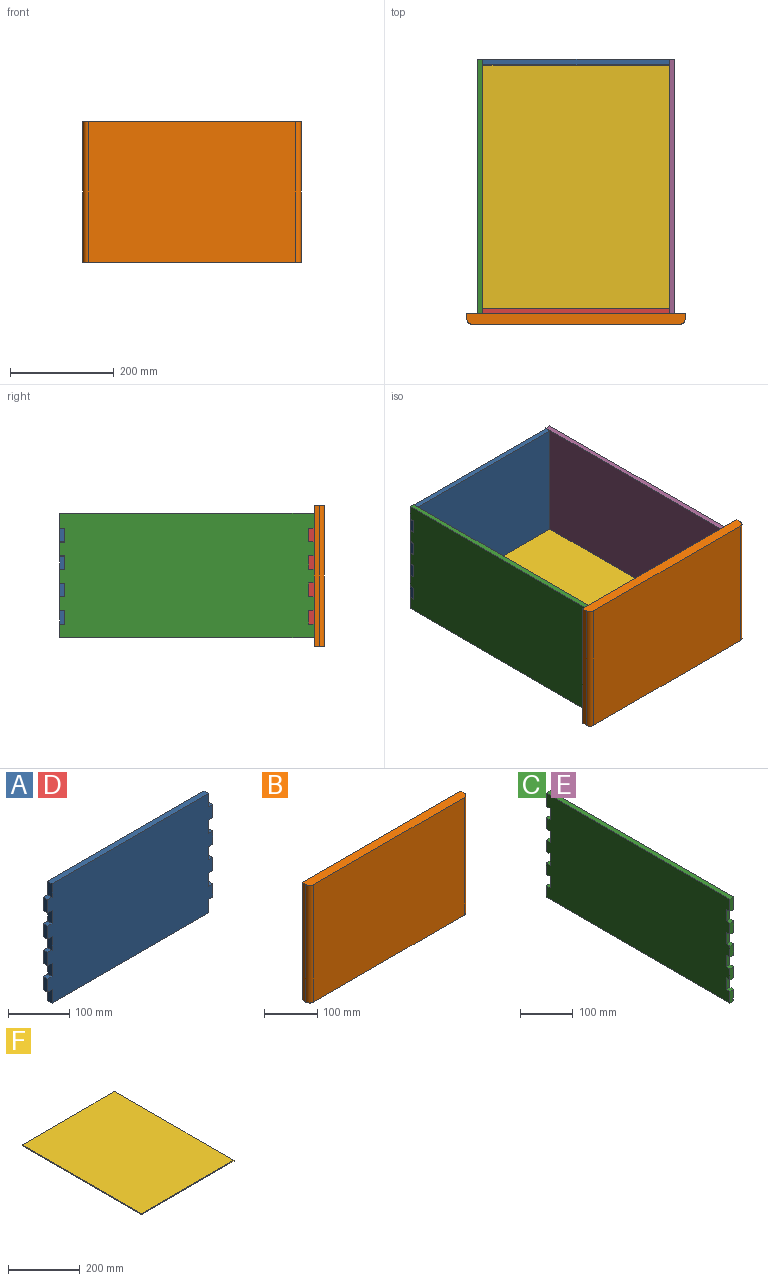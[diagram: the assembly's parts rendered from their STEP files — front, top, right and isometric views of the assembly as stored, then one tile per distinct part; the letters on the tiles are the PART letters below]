
ASSEMBLY  parts=6 mates=5
PART A: 38 faces, bbox 380x10x238 mm
  f0: plane 380x238mm, normal (0,-1,0), area 87792mm2, adj f2,f3,f4,f5,f6,f7,f8,f9
  f1: plane 380x238mm, normal (0,1,0), area 87792mm2, adj f2,f3,f4,f5,f6,f7,f8,f9
  f2: plane 360x10mm, normal (0,0,1), area 3600mm2, adj f0,f1,f13,f26
  f3: plane 26.4x10mm, normal (-1,0,0), area 264mm2, adj f0,f1,f33,f36
  f4: plane 26.4x10mm, normal (-1,0,0), area 264mm2, adj f0,f1,f30,f34
  f5: plane 26.4x10mm, normal (-1,0,0), area 264mm2, adj f0,f1,f27,f31
  f6: plane 26.4x10mm, normal (-1,0,0), area 264mm2, adj f0,f1,f25,f28
  f7: plane 360x10mm, normal (0,0,-1), area 3600mm2, adj f0,f1,f24,f37
  f8: plane 26.4x10mm, normal (1,0,0), area 264mm2, adj f0,f1,f21,f23
  f9: plane 26.4x10mm, normal (1,0,0), area 264mm2, adj f0,f1,f18,f20
  f10: plane 26.4x10mm, normal (1,0,0), area 264mm2, adj f0,f1,f15,f17
  f11: plane 26.4x10mm, normal (1,0,0), area 264mm2, adj f0,f1,f12,f14
  f12: plane 10x10mm, normal (0,0,1), area 100mm2, adj f0,f1,f11,f13
  f13: plane 26.8x10mm, normal (1,0,0), area 268mm2, adj f0,f1,f2,f12
  f14: plane 10x10mm, normal (0,0,-1), area 100mm2, adj f0,f1,f11,f16
  f15: plane 10x10mm, normal (0,0,1), area 100mm2, adj f0,f1,f10,f16
  f16: plane 26.4x10mm, normal (1,0,0), area 264mm2, adj f0,f1,f14,f15
  f17: plane 10x10mm, normal (0,0,-1), area 100mm2, adj f0,f1,f10,f19
  f18: plane 10x10mm, normal (0,0,1), area 100mm2, adj f0,f1,f9,f19
  f19: plane 26.4x10mm, normal (1,0,0), area 264mm2, adj f0,f1,f17,f18
  f20: plane 10x10mm, normal (0,0,-1), area 100mm2, adj f0,f1,f9,f22
  f21: plane 10x10mm, normal (0,0,1), area 100mm2, adj f0,f1,f8,f22
  f22: plane 26.4x10mm, normal (1,0,0), area 264mm2, adj f0,f1,f20,f21
  f23: plane 10x10mm, normal (0,0,-1), area 100mm2, adj f0,f1,f8,f24
  f24: plane 26.4x10mm, normal (1,0,0), area 264mm2, adj f0,f1,f7,f23
  f25: plane 10x10mm, normal (0,0,1), area 100mm2, adj f0,f1,f6,f26
  f26: plane 26.8x10mm, normal (-1,0,0), area 268mm2, adj f0,f1,f2,f25
  f27: plane 10x10mm, normal (0,0,1), area 100mm2, adj f0,f1,f5,f29
  f28: plane 10x10mm, normal (0,0,-1), area 100mm2, adj f0,f1,f6,f29
  f29: plane 26.4x10mm, normal (-1,0,0), area 264mm2, adj f0,f1,f27,f28
  f30: plane 10x10mm, normal (0,0,1), area 100mm2, adj f0,f1,f4,f32
  f31: plane 10x10mm, normal (0,0,-1), area 100mm2, adj f0,f1,f5,f32
  f32: plane 26.4x10mm, normal (-1,0,0), area 264mm2, adj f0,f1,f30,f31
  f33: plane 10x10mm, normal (0,0,1), area 100mm2, adj f0,f1,f3,f35
  f34: plane 10x10mm, normal (0,0,-1), area 100mm2, adj f0,f1,f4,f35
  f35: plane 26.4x10mm, normal (-1,0,0), area 264mm2, adj f0,f1,f33,f34
  f36: plane 10x10mm, normal (0,0,-1), area 100mm2, adj f0,f1,f3,f37
  f37: plane 26.4x10mm, normal (-1,0,0), area 264mm2, adj f0,f1,f7,f36
PART B: 8 faces, bbox 420x20x270 mm
  f0: plane 270x10mm, normal (-1,0,0), area 2700mm2, adj f1,f3,f5,f7
  f1: plane 420x20mm, normal (0,0,-1), area 8357.1mm2, adj f0,f2,f4,f5,f6,f7
  f2: plane 270x10mm, normal (1,0,0), area 2700mm2, adj f1,f3,f5,f6
  f3: plane 420x20mm, normal (0,0,1), area 8357.1mm2, adj f0,f2,f4,f5,f6,f7
  f4: plane 400x270mm, normal (0,-1,0), area 108000mm2, adj f1,f3,f6,f7
  f5: plane 420x270mm, normal (0,1,0), area 113400mm2, adj f0,f1,f2,f3
  f6: cylinder r=10mm len=270mm, axis (0,0,-1), area 4241.2mm2, adj f1,f2,f3,f4
  f7: cylinder r=10mm len=270mm, axis (0,0,1), area 4241.2mm2, adj f0,f1,f3,f4
PART C: 42 faces, bbox 10x490x240 mm
  f0: plane 490x4mm, normal (1,0,0), area 1960mm2, adj f1,f7,f13,f40
  f1: plane 26.4x10mm, normal (0,1,0), area 255mm2, adj f0,f6,f13,f14,f37,f39,f40,f41
  f2: plane 26.4x10mm, normal (0,1,0), area 264mm2, adj f6,f14,f34,f36
  f3: plane 26.4x10mm, normal (0,1,0), area 264mm2, adj f6,f14,f31,f33
  f4: plane 26.4x10mm, normal (0,1,0), area 264mm2, adj f6,f14,f28,f30
  f5: plane 30.4x10mm, normal (0,1,0), area 304mm2, adj f6,f11,f14,f27
  f6: plane 490x233mm, normal (1,0,0), area 112074mm2, adj f1,f2,f3,f4,f5,f7,f8,f9
  f7: plane 26.4x10mm, normal (0,-1,0), area 255mm2, adj f0,f6,f13,f14,f25,f39,f40,f41
  f8: plane 26.4x10mm, normal (0,-1,0), area 264mm2, adj f6,f14,f22,f24
  f9: plane 26.4x10mm, normal (0,-1,0), area 264mm2, adj f6,f14,f19,f21
  f10: plane 26.4x10mm, normal (0,-1,0), area 264mm2, adj f6,f14,f16,f18
  f11: plane 490x10mm, normal (0,0,1), area 4900mm2, adj f5,f6,f12,f14
  f12: plane 28.8x10mm, normal (0,-1,0), area 288mm2, adj f6,f11,f14,f15
  f13: plane 490x10mm, normal (0,0,-1), area 4900mm2, adj f0,f1,f7,f14
  f14: plane 490x240mm, normal (-1,0,0), area 115504mm2, adj f1,f2,f3,f4,f5,f7,f8,f9
  f15: plane 10x10mm, normal (0,0,-1), area 100mm2, adj f6,f12,f14,f17
  f16: plane 10x10mm, normal (0,0,1), area 100mm2, adj f6,f10,f14,f17
  f17: plane 26.4x10mm, normal (0,-1,0), area 264mm2, adj f6,f14,f15,f16
  f18: plane 10x10mm, normal (0,0,-1), area 100mm2, adj f6,f10,f14,f20
  f19: plane 10x10mm, normal (0,0,1), area 100mm2, adj f6,f9,f14,f20
  f20: plane 26.4x10mm, normal (0,-1,0), area 264mm2, adj f6,f14,f18,f19
  f21: plane 10x10mm, normal (0,0,-1), area 100mm2, adj f6,f9,f14,f23
  f22: plane 10x10mm, normal (0,0,1), area 100mm2, adj f6,f8,f14,f23
  f23: plane 26.4x10mm, normal (0,-1,0), area 264mm2, adj f6,f14,f21,f22
  f24: plane 10x10mm, normal (0,0,-1), area 100mm2, adj f6,f8,f14,f26
  f25: plane 10x10mm, normal (0,0,1), area 100mm2, adj f6,f7,f14,f26
  f26: plane 26.4x10mm, normal (0,-1,0), area 264mm2, adj f6,f14,f24,f25
  f27: plane 10x10mm, normal (0,0,-1), area 100mm2, adj f5,f6,f14,f29
  f28: plane 10x10mm, normal (0,0,1), area 100mm2, adj f4,f6,f14,f29
  f29: plane 26x10mm, normal (0,1,0), area 260mm2, adj f6,f14,f27,f28
  f30: plane 10x10mm, normal (0,0,-1), area 100mm2, adj f4,f6,f14,f32
  f31: plane 10x10mm, normal (0,0,1), area 100mm2, adj f3,f6,f14,f32
  f32: plane 26x10mm, normal (0,1,0), area 260mm2, adj f6,f14,f30,f31
  f33: plane 10x10mm, normal (0,0,-1), area 100mm2, adj f3,f6,f14,f35
  f34: plane 10x10mm, normal (0,0,1), area 100mm2, adj f2,f6,f14,f35
  f35: plane 26x10mm, normal (0,1,0), area 260mm2, adj f6,f14,f33,f34
  f36: plane 10x10mm, normal (0,0,-1), area 100mm2, adj f2,f6,f14,f38
  f37: plane 10x10mm, normal (0,0,1), area 100mm2, adj f1,f6,f14,f38
  f38: plane 26x10mm, normal (0,1,0), area 260mm2, adj f6,f14,f36,f37
  f39: plane 490x3mm, normal (0,0,-1), area 1470mm2, adj f1,f6,f7,f41
  f40: plane 490x3mm, normal (0,0,1), area 1470mm2, adj f0,f1,f7,f41
  f41: plane 490x3mm, normal (1,0,0), area 1470mm2, adj f1,f7,f39,f40
PART D: same geometry as A
PART E: same geometry as C
PART F: 6 faces, bbox 365x469x3 mm
  f0: plane 365x3mm, normal (0,-1,0), area 1095mm2, adj f1,f3,f4,f5
  f1: plane 469x3mm, normal (1,0,0), area 1407mm2, adj f0,f2,f4,f5
  f2: plane 365x3mm, normal (0,1,0), area 1095mm2, adj f1,f3,f4,f5
  f3: plane 469x3mm, normal (-1,0,0), area 1407mm2, adj f0,f2,f4,f5
  f4: plane 469x365mm, normal (0,0,1), area 171185mm2, adj f0,f1,f2,f3
  f5: plane 469x365mm, normal (0,0,-1), area 171185mm2, adj f0,f1,f2,f3
PLACE A t=(-154.76,225.69,174.25)mm
PLACE B t=(-406.61,-264.31,76.12)mm
PLACE C t=(-386.61,-356.54,190.75)mm
PLACE D t=(-154.76,-254.31,174.45)mm
PLACE E rot(axis=(0,0,1),180deg) t=(-6.61,317.92,190.95)mm
PLACE F t=(69.98,-357.23,96.13)mm
MATE parallel B.f5 <-> D.f0  axis (0,1,0) through (-196.61,-264.31,211.12)mm
MATE parallel F.f3 <-> C.f41  axis (-1,0,0) through (-379.61,-19.31,97.63)mm
MATE parallel E.f38 <-> D.f1  axis (0,-1,0) through (-6.61,-254.31,131.73)mm
MATE parallel A.f0 <-> C.f38  axis (0,-1,0) through (-386.61,215.69,131.53)mm
MATE parallel C.f26 <-> D.f1  axis (0,-1,0) through (-386.61,-254.31,131.73)mm
